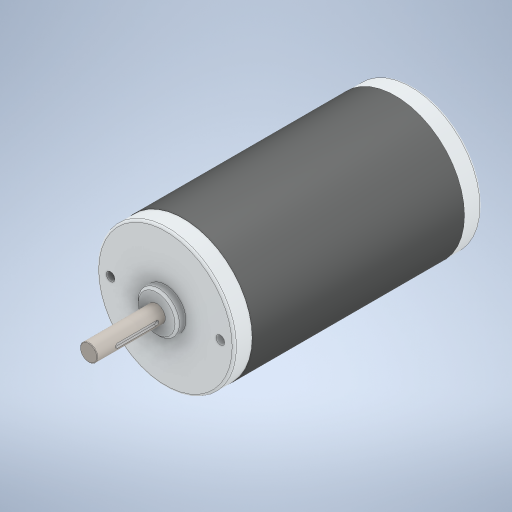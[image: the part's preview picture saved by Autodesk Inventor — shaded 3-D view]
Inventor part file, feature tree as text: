
AUTODESK INVENTOR PART (.ipt)
format: ipt  version: 2024.2 (Build 282272000, 272)  size: 315,904 bytes
history: native  units: in
note: dims shown in document units (in); Inventor stores cm internally (conversion verified against a paired STEP export)
features: fillet x1
ambient origin geometry x8: Origin, YZ Plane, XZ Plane, XY Plane, X Axis, Y Axis, Z Axis, Center Point
bodies: Solid1 (feature_tree)
feature tree (1):
  fillet  "Fillet5"  [1 undecoded]
note: 1 required parameter value undecoded (feature->parameter linkage not recoverable at this tier; creation-order binding heuristic only, values carry confidence <= 0.55)
